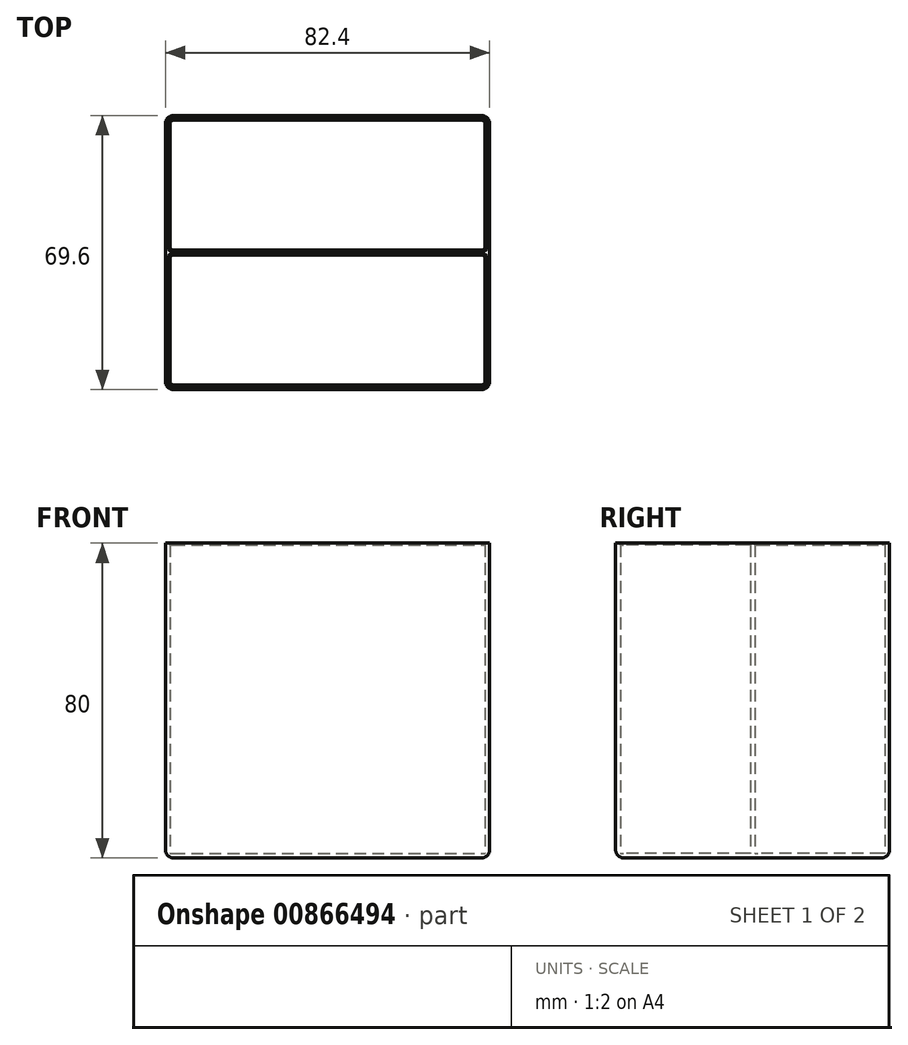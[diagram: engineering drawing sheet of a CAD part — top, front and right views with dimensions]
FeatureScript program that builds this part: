
annotation { "Feature Type Name" : "Feature", "Feature Type Description" : "" }
export const myFeature = defineFeature(function(context is Context, id is Id, definition is map)
    precondition{}
    {
        {
            var Q0;
            Q0=qCreatedBy(makeId("Top.planeOp"),FACE);
            var sketch = newSketch(context, id + "F0", { "sketchPlane" : qUnion([Q0])});
            skLineSegment(sketch, "E0.bottom", {"start": v(-39.2, 34.8) * mm, "end": v(39.2, 34.8) * mm});
            skLineSegment(sketch, "E0.top", {"start": v(-39.2, -34.8) * mm, "end": v(39.2, -34.8) * mm});
            skLineSegment(sketch, "E0.left", {"start": v(-41.2, 32.8) * mm, "end": v(-41.2, -32.8) * mm});
            skLineSegment(sketch, "E0.right", {"start": v(41.2, 32.8) * mm, "end": v(41.2, -32.8) * mm});
            skPoint(sketch, "E1.visualSharp", {"position": v(-41.2, 34.8) * mm});
            skArc(sketch, "E1.filletArc", {"start": v(-39.2, 34.8) * mm, "mid": v(-40.61, 34.21) * mm, "end": v(-41.2, 32.8) * mm});
            skPoint(sketch, "E2.visualSharp", {"position": v(41.2, 34.8) * mm});
            skArc(sketch, "E2.filletArc", {"start": v(41.2, 32.8) * mm, "mid": v(40.61, 34.21) * mm, "end": v(39.2, 34.8) * mm});
            skPoint(sketch, "E3.visualSharp", {"position": v(41.2, -34.8) * mm});
            skArc(sketch, "E3.filletArc", {"start": v(39.2, -34.8) * mm, "mid": v(40.61, -34.21) * mm, "end": v(41.2, -32.8) * mm});
            skPoint(sketch, "E4.visualSharp", {"position": v(-41.2, -34.8) * mm});
            skArc(sketch, "E4.filletArc", {"start": v(-41.2, -32.8) * mm, "mid": v(-40.61, -34.21) * mm, "end": v(-39.2, -34.8) * mm});
            skArc(sketch, "E5.0", {"start": v(-39.2, 33.6) * mm, "mid": v(-39.77, 33.37) * mm, "end": v(-40, 32.8) * mm});
            skLineSegment(sketch, "E5.1", {"start": v(-40, 32.8) * mm, "end": v(-40, 1.4) * mm});
            skLineSegment(sketch, "E5.2", {"start": v(-39.2, 33.6) * mm, "end": v(39.2, 33.6) * mm});
            skArc(sketch, "E5.3", {"start": v(-40, -32.8) * mm, "mid": v(-39.77, -33.37) * mm, "end": v(-39.2, -33.6) * mm});
            skArc(sketch, "E5.4", {"start": v(40, 32.8) * mm, "mid": v(39.77, 33.37) * mm, "end": v(39.2, 33.6) * mm});
            skLineSegment(sketch, "E5.5", {"start": v(40, 32.8) * mm, "end": v(40, 1.4) * mm});
            skArc(sketch, "E5.6", {"start": v(39.2, -33.6) * mm, "mid": v(39.77, -33.37) * mm, "end": v(40, -32.8) * mm});
            skLineSegment(sketch, "E5.7", {"start": v(-39.2, -33.6) * mm, "end": v(39.2, -33.6) * mm});
            skLineSegment(sketch, "E6", {"start": v(41.2, 0) * mm, "end": v(-41.2, 0) * mm, "construction": true});
            skLineSegment(sketch, "E7.bottom", {"start": v(39.2, 0.6) * mm, "end": v(-39.2, 0.6) * mm});
            skLineSegment(sketch, "E7.top", {"start": v(39.2, -0.6) * mm, "end": v(-39.2, -0.6) * mm});
            skPoint(sketch, "E8", {"position": v(-40, 0) * mm});
            skLineSegment(sketch, "E9.trimOffspring", {"start": v(40, -1.4) * mm, "end": v(40, -32.8) * mm});
            skLineSegment(sketch, "E10.trimOffspring", {"start": v(-40, -1.4) * mm, "end": v(-40, -32.8) * mm});
            skPoint(sketch, "E11.visualSharp", {"position": v(40, 0.6) * mm});
            skArc(sketch, "E11.filletArc", {"start": v(39.2, 0.6) * mm, "mid": v(39.77, 0.83) * mm, "end": v(40, 1.4) * mm});
            skPoint(sketch, "E12.visualSharp", {"position": v(40, -0.6) * mm});
            skArc(sketch, "E12.filletArc", {"start": v(40, -1.4) * mm, "mid": v(39.77, -0.83) * mm, "end": v(39.2, -0.6) * mm});
            skPoint(sketch, "E13.visualSharp", {"position": v(-40, -0.6) * mm});
            skArc(sketch, "E13.filletArc", {"start": v(-39.2, -0.6) * mm, "mid": v(-39.77, -0.83) * mm, "end": v(-40, -1.4) * mm});
            skPoint(sketch, "E14.visualSharp", {"position": v(-40, 0.6) * mm});
            skArc(sketch, "E14.filletArc", {"start": v(-40, 1.4) * mm, "mid": v(-39.77, 0.83) * mm, "end": v(-39.2, 0.6) * mm});
            skSolve(sketch);
        }
        {
            var Q0;
            Q0 = qSketchRegion(id + "F0", true);
            extrude(context, id + "F1", {"entities" : qUnion([Q0]), "depth" : 80 * mm, "offsetDistance" : 25 * mm});
        }
        {
            var Q0;
            Q0=qCreatedBy(makeId("Top.planeOp"),FACE);
            var sketch = newSketch(context, id + "F2", { "sketchPlane" : qUnion([Q0])});
            skLineSegment(sketch, "E15.0", {"start": v(-41.2, 32.8) * mm, "end": v(-41.2, -32.8) * mm});
            skArc(sketch, "E16.0", {"start": v(-39.2, 34.8) * mm, "mid": v(-40.61, 34.21) * mm, "end": v(-41.2, 32.8) * mm});
            skLineSegment(sketch, "E17.0", {"start": v(-39.2, 34.8) * mm, "end": v(39.2, 34.8) * mm});
            skArc(sketch, "E18.0", {"start": v(41.2, 32.8) * mm, "mid": v(40.61, 34.21) * mm, "end": v(39.2, 34.8) * mm});
            skLineSegment(sketch, "E19.0", {"start": v(41.2, 32.8) * mm, "end": v(41.2, -32.8) * mm});
            skArc(sketch, "E20.0", {"start": v(39.2, -34.8) * mm, "mid": v(40.61, -34.21) * mm, "end": v(41.2, -32.8) * mm});
            skLineSegment(sketch, "E21.0", {"start": v(-39.2, -34.8) * mm, "end": v(39.2, -34.8) * mm});
            skArc(sketch, "E22.0", {"start": v(-41.2, -32.8) * mm, "mid": v(-40.61, -34.21) * mm, "end": v(-39.2, -34.8) * mm});
            skSolve(sketch);
        }
        {
            var Q0;
            Q0 = qSketchRegion(id + "F2", true);
            extrude(context, id + "F3", {"entities" : qUnion([Q0]), "operationType" : NewBodyOperationType.ADD, "depth" : 1.2 * mm, "offsetDistance" : 25 * mm});
        }
        {
            var Q0;
            Q0=makeQuery(id+"F1.opExtrude","CAP_EDGE",EDGE,{"disambiguationData":[OSD([sQuery(id+"F0.wireOp",EDGE,"E0.right")])],"isStart":true});
            var Q1;
            Q1=makeQuery(id+"F1.opExtrude","CAP_EDGE",EDGE,{"disambiguationData":[OSD([sQuery(id+"F0.wireOp",EDGE,"E0.bottom")])],"isStart":true});
            var Q2;
            Q2=makeQuery(id+"F1.opExtrude","CAP_EDGE",EDGE,{"disambiguationData":[OSD([sQuery(id+"F0.wireOp",EDGE,"E0.top")])],"isStart":true});
            var Q3;
            Q3=makeQuery(id+"F1.opExtrude","CAP_EDGE",EDGE,{"disambiguationData":[OSD([sQuery(id+"F0.wireOp",EDGE,"E0.left")])],"isStart":true});
            fillet(context, id + "F4", {"entities" : qUnion([Q0, Q1, Q2, Q3]), "radius" : 2 * mm, "tangentPropagation" : true, "allowEdgeOverflow" : false});
        }
        {
            var Q0;
            Q0=makeQuery(id+"F1.opExtrude","CAP_EDGE",EDGE,{"disambiguationData":[OSD([sQuery(id+"F0.wireOp",EDGE,"E5.2")])],"isStart":false});
            var Q1;
            Q1=makeQuery(id+"F1.opExtrude","CAP_EDGE",EDGE,{"disambiguationData":[OSD([sQuery(id+"F0.wireOp",EDGE,"E7.top")])],"isStart":false});
            chamfer(context, id + "F5", {"entities" : qUnion([Q0, Q1]), "width" : 0.5 * mm, "tangentPropagation" : true});
        }
    });
